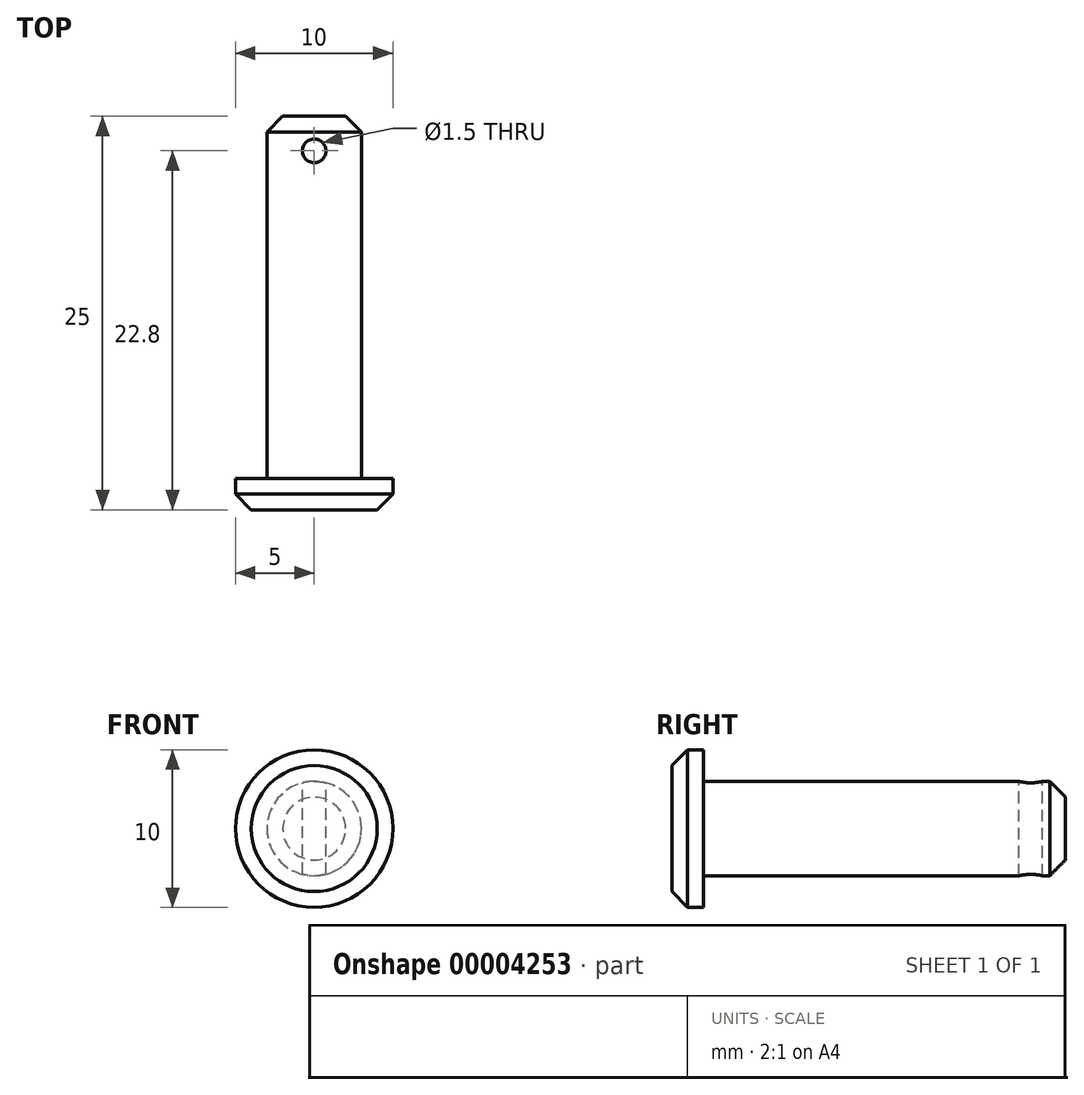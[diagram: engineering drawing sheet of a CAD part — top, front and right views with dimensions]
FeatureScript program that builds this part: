
annotation { "Feature Type Name" : "Feature", "Feature Type Description" : "" }
export const myFeature = defineFeature(function(context is Context, id is Id, definition is map)
    precondition{}
    {
        {
            var Q0;
            Q0=qCreatedBy(makeId("Right.planeOp"),FACE);
            var sketch = newSketch(context, id + "F0", { "sketchPlane" : qUnion([Q0])});
            skLineSegment(sketch, "E0", {"start": v(0, 0) * mm, "end": v(0, 5) * mm});
            skLineSegment(sketch, "E1", {"start": v(0, 5) * mm, "end": v(2, 5) * mm});
            skLineSegment(sketch, "E2", {"start": v(2, 5) * mm, "end": v(2, 3) * mm});
            skLineSegment(sketch, "E3", {"start": v(2, 3) * mm, "end": v(25, 3) * mm});
            skLineSegment(sketch, "E4", {"start": v(25, 3) * mm, "end": v(25, 0) * mm});
            skLineSegment(sketch, "E5", {"start": v(25, 0) * mm, "end": v(0, 0) * mm});
            skSolve(sketch);
        }
        {
            var Q0;
            Q0=makeQuery(id+"F0.imprint","IMPRINT",FACE,{"disambiguationData":[TD([[makeQuery(id+"F0.imprint","IMPRINT",EDGE,{"derivedFrom":sQuery(id+"F0.wireOp",EDGE,"E0")}),-1.0]])]});
            var Q1;
            Q1=sQuery(id+"F0.wireOp",EDGE,"E5");
            revolve(context, id + "F1", {"entities" : qUnion([Q0]), "axis" : qUnion([Q1]), "revolveType" : RevolveType.FULL});
        }
        {
            var Q0;
            Q0=makeQuery(id+"F1.opRevolve","SWEPT_EDGE",EDGE,{"disambiguationData":[OSD([sQuery(id+"F0.wireOp",EDGE,"E0"),sQuery(id+"F0.wireOp",EDGE,"E1")])]});
            var Q1;
            Q1=makeQuery(id+"F1.opRevolve","SWEPT_EDGE",EDGE,{"disambiguationData":[OSD([sQuery(id+"F0.wireOp",EDGE,"E3"),sQuery(id+"F0.wireOp",EDGE,"E4")])]});
            chamfer(context, id + "F2", {"entities" : qUnion([Q0, Q1]), "width" : 1 * mm, "tangentPropagation" : true});
        }
        {
            var Q0;
            Q0=qCreatedBy(makeId("Top.planeOp"),FACE);
            var sketch = newSketch(context, id + "F3", { "sketchPlane" : qUnion([Q0])});
            skCircle(sketch, "E6", {"center": v(0, 22.8) * mm, "radius": 0.75 * mm});
            skSolve(sketch);
        }
        {
            var Q0;
            Q0 = qSketchRegion(id + "F3", true);
            extrude(context, id + "F4", {"entities" : qUnion([Q0]), "operationType" : NewBodyOperationType.REMOVE, "endBound" : BoundingType.THROUGH_ALL, "oppositeDirection" : true, "depth" : 25 * mm});
        }
        {
            var Q0;
            Q0 = qSketchRegion(id + "F3", true);
            extrude(context, id + "F5", {"entities" : qUnion([Q0]), "operationType" : NewBodyOperationType.REMOVE, "endBound" : BoundingType.THROUGH_ALL, "depth" : 25 * mm});
        }
    });
